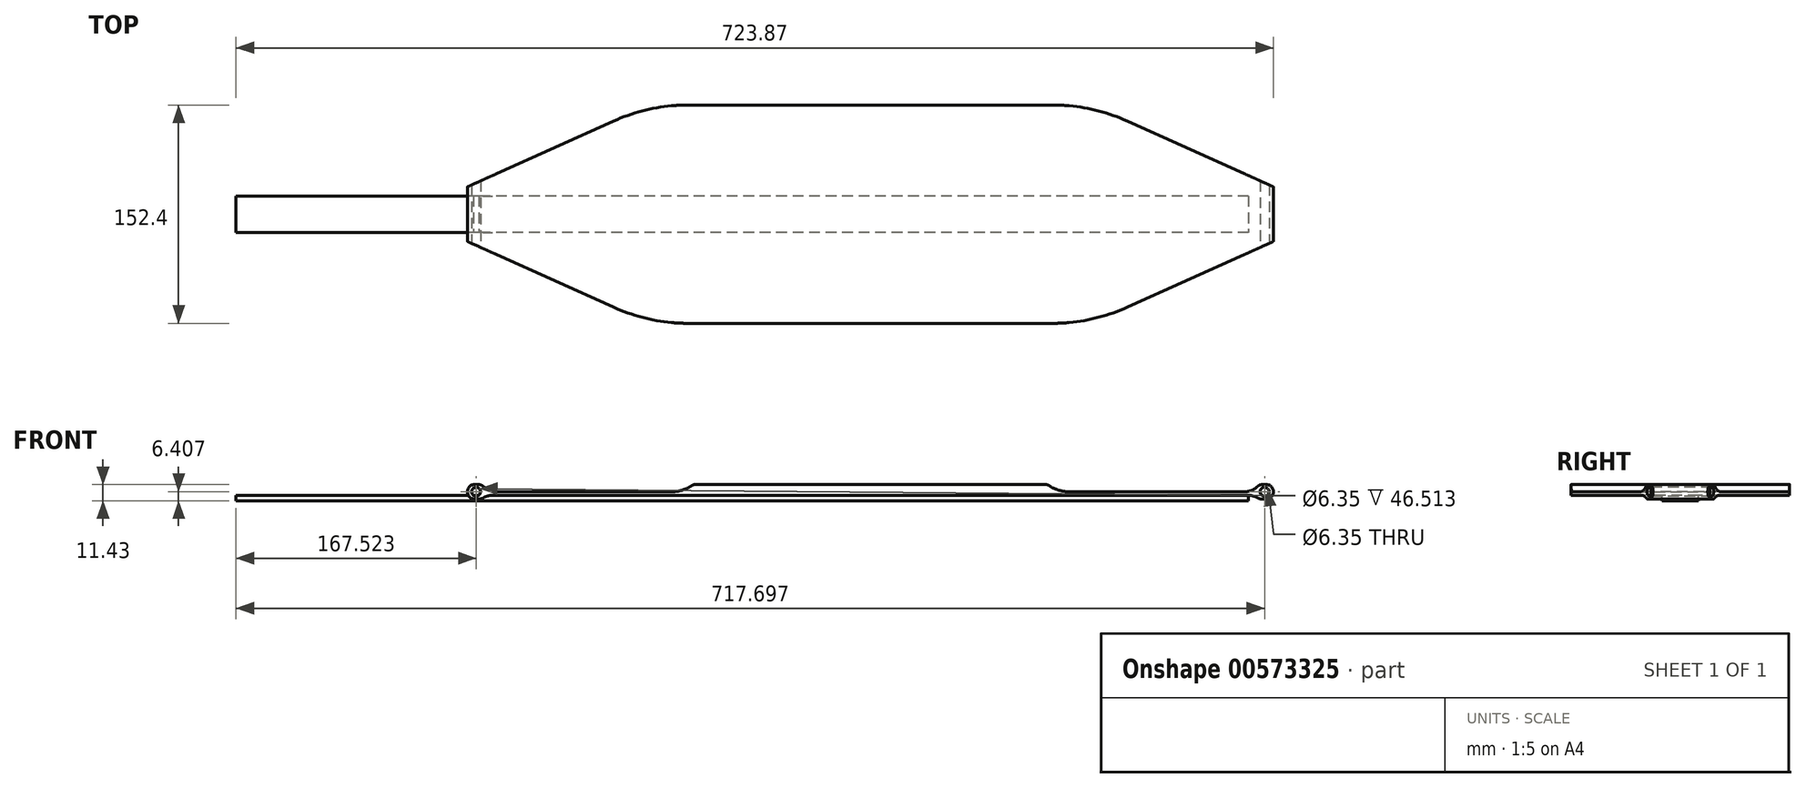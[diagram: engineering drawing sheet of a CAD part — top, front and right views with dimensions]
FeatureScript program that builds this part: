
annotation { "Feature Type Name" : "Feature", "Feature Type Description" : "" }
export const myFeature = defineFeature(function(context is Context, id is Id, definition is map)
    precondition{}
    {
        {
            var Q0;
            Q0=qCreatedBy(makeId("Top.planeOp"),FACE);
            var sketch = newSketch(context, id + "F0", { "sketchPlane" : qUnion([Q0])});
            skLineSegment(sketch, "E0", {"start": v(0, 76.2) * mm, "end": v(-127, 76.2) * mm});
            skLineSegment(sketch, "E1", {"start": v(-179.12, 65.01) * mm, "end": v(-281.26, 19.05) * mm});
            skLineSegment(sketch, "E2", {"start": v(-281.26, 19.05) * mm, "end": v(-281.26, 0) * mm});
            skLineSegment(sketch, "E3", {"start": v(-281.26, 0) * mm, "end": v(-281.26, -19.05) * mm});
            skLineSegment(sketch, "E4", {"start": v(-281.26, -19.05) * mm, "end": v(-179.12, -65.01) * mm});
            skLineSegment(sketch, "E5", {"start": v(-127, -76.2) * mm, "end": v(0, -76.2) * mm});
            skPoint(sketch, "E6.visualSharp", {"position": v(-154.26, 76.2) * mm});
            skArc(sketch, "E6.filletArc", {"start": v(-127, 76.2) * mm, "mid": v(-153.65, 73.37) * mm, "end": v(-179.12, 65.01) * mm});
            skPoint(sketch, "E7.visualSharp", {"position": v(-154.26, -76.2) * mm});
            skArc(sketch, "E7.filletArc", {"start": v(-179.12, -65.01) * mm, "mid": v(-153.65, -73.37) * mm, "end": v(-127, -76.2) * mm});
            skLineSegment(sketch, "E8.MirrorCS", {"start": v(0, 76.2) * mm, "end": v(127, 76.2) * mm});
            skLineSegment(sketch, "E9.MirrorCS", {"start": v(179.12, 65.01) * mm, "end": v(281.26, 19.05) * mm});
            skLineSegment(sketch, "E10.MirrorCS", {"start": v(281.26, 19.05) * mm, "end": v(281.26, 0) * mm});
            skLineSegment(sketch, "E11.MirrorCS", {"start": v(281.26, 0) * mm, "end": v(281.26, -19.05) * mm});
            skPoint(sketch, "E12.MirrorP", {"position": v(154.26, -76.2) * mm});
            skLineSegment(sketch, "E13.MirrorCS", {"start": v(281.26, -19.05) * mm, "end": v(179.12, -65.01) * mm});
            skArc(sketch, "E14.MirrorCS", {"start": v(179.12, -65.01) * mm, "mid": v(153.65, -73.37) * mm, "end": v(127, -76.2) * mm});
            skLineSegment(sketch, "E15.MirrorCS", {"start": v(127, -76.2) * mm, "end": v(0, -76.2) * mm});
            skArc(sketch, "E16.MirrorCS", {"start": v(127, 76.2) * mm, "mid": v(153.65, 73.37) * mm, "end": v(179.12, 65.01) * mm});
            skPoint(sketch, "E17.MirrorP", {"position": v(154.26, 76.2) * mm});
            skSolve(sketch);
        }
        {
            var Q0;
            Q0 = qSketchRegion(id + "F0", true);
            extrude(context, id + "F1", {"entities" : qUnion([Q0]), "depth" : 2.54 * mm, "offsetDistance" : 25.4 * mm});
        }
        {
            var Q0;
            Q0=makeQuery(id+"F1.opExtrude","CAP_FACE",FACE,{"disambiguationData":[OSD([sQuery(id+"F0.wireOp",EDGE,"E0"),sQuery(id+"F0.wireOp",EDGE,"E1"),sQuery(id+"F0.wireOp",EDGE,"E2"),sQuery(id+"F0.wireOp",EDGE,"E3"),sQuery(id+"F0.wireOp",EDGE,"E4"),sQuery(id+"F0.wireOp",EDGE,"E5"),sQuery(id+"F0.wireOp",EDGE,"E6.filletArc"),sQuery(id+"F0.wireOp",EDGE,"E7.filletArc"),sQuery(id+"F0.wireOp",EDGE,"E8.MirrorCS"),sQuery(id+"F0.wireOp",EDGE,"E9.MirrorCS"),sQuery(id+"F0.wireOp",EDGE,"E10.MirrorCS"),sQuery(id+"F0.wireOp",EDGE,"E11.MirrorCS"),sQuery(id+"F0.wireOp",EDGE,"E13.MirrorCS"),sQuery(id+"F0.wireOp",EDGE,"E14.MirrorCS"),sQuery(id+"F0.wireOp",EDGE,"E15.MirrorCS"),sQuery(id+"F0.wireOp",EDGE,"E16.MirrorCS")])],"isStart":false});
            var sketch = newSketch(context, id + "F2", { "sketchPlane" : qUnion([Q0])});
            skLineSegment(sketch, "E18", {"start": v(0, 76.2) * mm, "end": v(-127, 76.2) * mm});
            skLineSegment(sketch, "E19", {"start": v(-127, -76.2) * mm, "end": v(0, -76.2) * mm});
            skLineSegment(sketch, "E20.MirrorCS", {"start": v(127, -76.2) * mm, "end": v(0, -76.2) * mm});
            skLineSegment(sketch, "E21.MirrorCS", {"start": v(0, 76.2) * mm, "end": v(127, 76.2) * mm});
            skLineSegment(sketch, "E22", {"start": v(-127, 76.2) * mm, "end": v(-127, -76.2) * mm});
            skLineSegment(sketch, "E23", {"start": v(127, 76.2) * mm, "end": v(127, -76.2) * mm});
            skSolve(sketch);
        }
        {
            var Q0;
            Q0 = qSketchRegion(id + "F2", true);
            extrude(context, id + "F3", {"entities" : qUnion([Q0]), "operationType" : NewBodyOperationType.ADD, "depth" : 5.08 * mm, "offsetDistance" : 25.4 * mm});
        }
        {
            var Q0;
            Q0=makeQuery(id+"F3.opExtrude","CAP_EDGE",EDGE,{"disambiguationData":[OSD([sQuery(id+"F2.wireOp",EDGE,"E22")])],"isStart":false});
            var Q1;
            Q1=makeQuery(id+"F3.opExtrude","CAP_EDGE",EDGE,{"disambiguationData":[OSD([sQuery(id+"F2.wireOp",EDGE,"E23")])],"isStart":false});
            fillet(context, id + "F4", {"entities" : qUnion([Q0, Q1]), "radius" : 5.08 * mm, "tangentPropagation" : true, "allowEdgeOverflow" : false});
        }
        {
            var Q0;
            {var subQ0=sQuery(id+"F0.wireOp",EDGE,"E4");var subQ1=sQuery(id+"F2.wireOp",EDGE,"E22");var subQ2=sQuery(id+"F0.wireOp",EDGE,"E3");var subQ3=sQuery(id+"F0.wireOp",EDGE,"E2");var subQ4=sQuery(id+"F0.wireOp",EDGE,"E1");var subQ5=sQuery(id+"F0.wireOp",EDGE,"E8.MirrorCS");var subQ6=sQuery(id+"F0.wireOp",EDGE,"E0");var subQ7=sQuery(id+"F0.wireOp",EDGE,"E15.MirrorCS");var subQ8=sQuery(id+"F0.wireOp",EDGE,"E5");var subQ9=sQuery(id+"F0.wireOp",EDGE,"E6.filletArc");var subQ10=sQuery(id+"F0.wireOp",EDGE,"E7.filletArc");Q0=makeQuery(id+"F4.opFillet","BLEND_EDGE",EDGE,{"blendedFrom":[makeQuery(id+"F3.opExtrude","CAP_EDGE",EDGE,{"disambiguationData":[OSD([subQ1])],"isStart":false}),makeQuery(id+"F3.boolean.opBoolean","SPLIT",FACE,{"disambiguationData":[TD([makeQuery(id+"F1.opExtrude","SWEPT_FACE",FACE,{"disambiguationData":[OSD([subQ4])]})])],"derivedFrom":makeQuery(id+"F1.opExtrude","CAP_FACE",FACE,{"disambiguationData":[OSD([subQ6,subQ4,subQ3,subQ2,subQ0,subQ8,subQ9,subQ10,subQ5,sQuery(id+"F0.wireOp",EDGE,"E9.MirrorCS"),sQuery(id+"F0.wireOp",EDGE,"E10.MirrorCS"),sQuery(id+"F0.wireOp",EDGE,"E11.MirrorCS"),sQuery(id+"F0.wireOp",EDGE,"E13.MirrorCS"),sQuery(id+"F0.wireOp",EDGE,"E14.MirrorCS"),subQ7,sQuery(id+"F0.wireOp",EDGE,"E16.MirrorCS")])],"isStart":false})})],"blendedInto":[makeQuery(id+"F3.boolean.opBoolean","SPLIT",FACE,{"disambiguationData":[TD([makeQuery(id+"F1.opExtrude","SWEPT_FACE",FACE,{"disambiguationData":[OSD([subQ4])]})])],"derivedFrom":makeQuery(id+"F1.opExtrude","CAP_FACE",FACE,{"disambiguationData":[OSD([subQ6,subQ4,subQ3,subQ2,subQ0,subQ8,subQ9,subQ10,subQ5,sQuery(id+"F0.wireOp",EDGE,"E9.MirrorCS"),sQuery(id+"F0.wireOp",EDGE,"E10.MirrorCS"),sQuery(id+"F0.wireOp",EDGE,"E11.MirrorCS"),sQuery(id+"F0.wireOp",EDGE,"E13.MirrorCS"),sQuery(id+"F0.wireOp",EDGE,"E14.MirrorCS"),subQ7,sQuery(id+"F0.wireOp",EDGE,"E16.MirrorCS")])],"isStart":false})})]});}
            var Q1;
            {var subQ0=sQuery(id+"F0.wireOp",EDGE,"E11.MirrorCS");var subQ1=sQuery(id+"F0.wireOp",EDGE,"E10.MirrorCS");var subQ2=sQuery(id+"F0.wireOp",EDGE,"E9.MirrorCS");var subQ3=sQuery(id+"F0.wireOp",EDGE,"E15.MirrorCS");var subQ4=sQuery(id+"F0.wireOp",EDGE,"E5");var subQ5=sQuery(id+"F2.wireOp",EDGE,"E23");var subQ6=sQuery(id+"F0.wireOp",EDGE,"E8.MirrorCS");var subQ7=sQuery(id+"F0.wireOp",EDGE,"E0");var subQ8=sQuery(id+"F0.wireOp",EDGE,"E16.MirrorCS");var subQ9=sQuery(id+"F0.wireOp",EDGE,"E13.MirrorCS");var subQ10=sQuery(id+"F0.wireOp",EDGE,"E14.MirrorCS");Q1=makeQuery(id+"F4.opFillet","BLEND_EDGE",EDGE,{"blendedFrom":[makeQuery(id+"F3.opExtrude","CAP_EDGE",EDGE,{"disambiguationData":[OSD([subQ5])],"isStart":false}),makeQuery(id+"F3.boolean.opBoolean","SPLIT",FACE,{"disambiguationData":[TD([makeQuery(id+"F1.opExtrude","SWEPT_FACE",FACE,{"disambiguationData":[OSD([subQ2])]})])],"derivedFrom":makeQuery(id+"F1.opExtrude","CAP_FACE",FACE,{"disambiguationData":[OSD([subQ7,sQuery(id+"F0.wireOp",EDGE,"E1"),sQuery(id+"F0.wireOp",EDGE,"E2"),sQuery(id+"F0.wireOp",EDGE,"E3"),sQuery(id+"F0.wireOp",EDGE,"E4"),subQ4,sQuery(id+"F0.wireOp",EDGE,"E6.filletArc"),sQuery(id+"F0.wireOp",EDGE,"E7.filletArc"),subQ6,subQ2,subQ1,subQ0,subQ9,subQ10,subQ3,subQ8])],"isStart":false})})],"blendedInto":[makeQuery(id+"F3.boolean.opBoolean","SPLIT",FACE,{"disambiguationData":[TD([makeQuery(id+"F1.opExtrude","SWEPT_FACE",FACE,{"disambiguationData":[OSD([subQ2])]})])],"derivedFrom":makeQuery(id+"F1.opExtrude","CAP_FACE",FACE,{"disambiguationData":[OSD([subQ7,sQuery(id+"F0.wireOp",EDGE,"E1"),sQuery(id+"F0.wireOp",EDGE,"E2"),sQuery(id+"F0.wireOp",EDGE,"E3"),sQuery(id+"F0.wireOp",EDGE,"E4"),subQ4,sQuery(id+"F0.wireOp",EDGE,"E6.filletArc"),sQuery(id+"F0.wireOp",EDGE,"E7.filletArc"),subQ6,subQ2,subQ1,subQ0,subQ9,subQ10,subQ3,subQ8])],"isStart":false})})]});}
            fillet(context, id + "F5", {"entities" : qUnion([Q0, Q1]), "radius" : 25.4 * mm, "tangentPropagation" : true, "allowEdgeOverflow" : false});
        }
        {
            var Q0;
            {var subQ0=sQuery(id+"F0.wireOp",EDGE,"E4");var subQ1=sQuery(id+"F0.wireOp",EDGE,"E3");var subQ2=sQuery(id+"F0.wireOp",EDGE,"E2");var subQ3=sQuery(id+"F0.wireOp",EDGE,"E1");var subQ4=sQuery(id+"F0.wireOp",EDGE,"E8.MirrorCS");var subQ5=sQuery(id+"F0.wireOp",EDGE,"E0");var subQ6=sQuery(id+"F0.wireOp",EDGE,"E15.MirrorCS");var subQ7=sQuery(id+"F0.wireOp",EDGE,"E5");var subQ8=sQuery(id+"F0.wireOp",EDGE,"E6.filletArc");var subQ9=sQuery(id+"F0.wireOp",EDGE,"E7.filletArc");Q0=makeQuery(id+"F3.boolean.opBoolean","SPLIT",FACE,{"disambiguationData":[TD([makeQuery(id+"F1.opExtrude","SWEPT_FACE",FACE,{"disambiguationData":[OSD([subQ3])]})])],"derivedFrom":makeQuery(id+"F1.opExtrude","CAP_FACE",FACE,{"disambiguationData":[OSD([subQ5,subQ3,subQ2,subQ1,subQ0,subQ7,subQ8,subQ9,subQ4,sQuery(id+"F0.wireOp",EDGE,"E9.MirrorCS"),sQuery(id+"F0.wireOp",EDGE,"E10.MirrorCS"),sQuery(id+"F0.wireOp",EDGE,"E11.MirrorCS"),sQuery(id+"F0.wireOp",EDGE,"E13.MirrorCS"),sQuery(id+"F0.wireOp",EDGE,"E14.MirrorCS"),subQ6,sQuery(id+"F0.wireOp",EDGE,"E16.MirrorCS")])],"isStart":false})});}
            var sketch = newSketch(context, id + "F6", { "sketchPlane" : qUnion([Q0])});
            skLineSegment(sketch, "E24", {"start": v(-281.26, 19.05) * mm, "end": v(-268.56, 24.76) * mm});
            skLineSegment(sketch, "E25", {"start": v(-268.56, 24.76) * mm, "end": v(-268.56, -24.76) * mm});
            skLineSegment(sketch, "E26", {"start": v(-268.56, -24.76) * mm, "end": v(-281.26, -19.05) * mm});
            skLineSegment(sketch, "E27", {"start": v(-281.26, -19.05) * mm, "end": v(-281.26, 19.05) * mm});
            skLineSegment(sketch, "E28.MirrorCS", {"start": v(268.56, 24.76) * mm, "end": v(268.56, -24.76) * mm});
            skLineSegment(sketch, "E29.MirrorCS", {"start": v(268.56, -24.76) * mm, "end": v(281.26, -19.05) * mm});
            skLineSegment(sketch, "E30.MirrorCS", {"start": v(281.26, -19.05) * mm, "end": v(281.26, 19.05) * mm});
            skLineSegment(sketch, "E31.MirrorCS", {"start": v(281.26, 19.05) * mm, "end": v(268.56, 24.76) * mm});
            skSolve(sketch);
        }
        {
            var Q0;
            Q0 = qSketchRegion(id + "F6", true);
            extrude(context, id + "F7", {"entities" : qUnion([Q0]), "operationType" : NewBodyOperationType.ADD, "depth" : 5.08 * mm, "offsetDistance" : 25.4 * mm, "hasSecondDirection" : true, "secondDirectionOppositeDirection" : true, "secondDirectionDepth" : 5.08 * mm});
        }
        {
            var Q0;
            Q0=qCreatedBy(makeId("Front.planeOp"),FACE);
            var sketch = newSketch(context, id + "F8", { "sketchPlane" : qUnion([Q0])});
            skCircle(sketch, "E32", {"center": v(-275.09, 2.6) * mm, "radius": 3.18 * mm});
            skCircle(sketch, "E33.MirrorC", {"center": v(275.09, 2.6) * mm, "radius": 3.18 * mm});
            skSolve(sketch);
        }
        {
            var Q0;
            Q0 = qSketchRegion(id + "F8", true);
            extrude(context, id + "F9", {"entities" : qUnion([Q0]), "operationType" : NewBodyOperationType.REMOVE, "endBound" : BoundingType.THROUGH_ALL, "oppositeDirection" : true, "depth" : 25.4 * mm, "offsetDistance" : 25.4 * mm, "hasSecondDirection" : true, "secondDirectionBound" : SecondDirectionBoundingType.THROUGH_ALL, "secondDirectionOppositeDirection" : false, "secondDirectionDepth" : 25.4 * mm});
        }
        {
            var Q0;
            Q0=makeQuery(id+"F7.opExtrude","CAP_EDGE",EDGE,{"disambiguationData":[OSD([sQuery(id+"F6.wireOp",EDGE,"E27")])],"isStart":false});
            var Q1;
            Q1=makeQuery(id+"F7.opExtrude","CAP_EDGE",EDGE,{"disambiguationData":[OSD([sQuery(id+"F6.wireOp",EDGE,"E27")])],"isStart":true});
            var Q2;
            Q2=makeQuery(id+"F7.opExtrude","CAP_EDGE",EDGE,{"disambiguationData":[OSD([sQuery(id+"F6.wireOp",EDGE,"E25")])],"isStart":true});
            var Q3;
            Q3=makeQuery(id+"F7.opExtrude","CAP_EDGE",EDGE,{"disambiguationData":[OSD([sQuery(id+"F6.wireOp",EDGE,"E25")])],"isStart":false});
            var Q4;
            Q4=makeQuery(id+"F7.opExtrude","CAP_EDGE",EDGE,{"disambiguationData":[OSD([sQuery(id+"F6.wireOp",EDGE,"E28.MirrorCS")])],"isStart":false});
            var Q5;
            Q5=makeQuery(id+"F7.opExtrude","CAP_EDGE",EDGE,{"disambiguationData":[OSD([sQuery(id+"F6.wireOp",EDGE,"E30.MirrorCS")])],"isStart":false});
            var Q6;
            Q6=makeQuery(id+"F7.opExtrude","CAP_EDGE",EDGE,{"disambiguationData":[OSD([sQuery(id+"F6.wireOp",EDGE,"E30.MirrorCS")])],"isStart":true});
            var Q7;
            Q7=makeQuery(id+"F7.opExtrude","CAP_EDGE",EDGE,{"disambiguationData":[OSD([sQuery(id+"F6.wireOp",EDGE,"E28.MirrorCS")])],"isStart":true});
            fillet(context, id + "F10", {"entities" : qUnion([Q0, Q1, Q2, Q3, Q4, Q5, Q6, Q7]), "radius" : 5.08 * mm, "tangentPropagation" : true, "allowEdgeOverflow" : false});
        }
        {
            var Q0;
            {var subQ0=sQuery(id+"F0.wireOp",EDGE,"E4");var subQ1=sQuery(id+"F0.wireOp",EDGE,"E3");var subQ2=sQuery(id+"F0.wireOp",EDGE,"E2");var subQ3=sQuery(id+"F0.wireOp",EDGE,"E1");var subQ4=sQuery(id+"F0.wireOp",EDGE,"E8.MirrorCS");var subQ5=sQuery(id+"F0.wireOp",EDGE,"E0");var subQ6=sQuery(id+"F0.wireOp",EDGE,"E15.MirrorCS");var subQ7=sQuery(id+"F0.wireOp",EDGE,"E5");var subQ8=sQuery(id+"F0.wireOp",EDGE,"E6.filletArc");var subQ9=sQuery(id+"F0.wireOp",EDGE,"E7.filletArc");Q0=makeQuery(id+"F10.opFillet","BLEND_EDGE",EDGE,{"blendedFrom":[makeQuery(id+"F7.opExtrude","CAP_EDGE",EDGE,{"disambiguationData":[OSD([sQuery(id+"F6.wireOp",EDGE,"E25")])],"isStart":false}),makeQuery(id+"F3.boolean.opBoolean","SPLIT",FACE,{"disambiguationData":[TD([makeQuery(id+"F1.opExtrude","SWEPT_FACE",FACE,{"disambiguationData":[OSD([subQ3])]})])],"derivedFrom":makeQuery(id+"F1.opExtrude","CAP_FACE",FACE,{"disambiguationData":[OSD([subQ5,subQ3,subQ2,subQ1,subQ0,subQ7,subQ8,subQ9,subQ4,sQuery(id+"F0.wireOp",EDGE,"E9.MirrorCS"),sQuery(id+"F0.wireOp",EDGE,"E10.MirrorCS"),sQuery(id+"F0.wireOp",EDGE,"E11.MirrorCS"),sQuery(id+"F0.wireOp",EDGE,"E13.MirrorCS"),sQuery(id+"F0.wireOp",EDGE,"E14.MirrorCS"),subQ6,sQuery(id+"F0.wireOp",EDGE,"E16.MirrorCS")])],"isStart":false})})],"blendedInto":[makeQuery(id+"F3.boolean.opBoolean","SPLIT",FACE,{"disambiguationData":[TD([makeQuery(id+"F1.opExtrude","SWEPT_FACE",FACE,{"disambiguationData":[OSD([subQ3])]})])],"derivedFrom":makeQuery(id+"F1.opExtrude","CAP_FACE",FACE,{"disambiguationData":[OSD([subQ5,subQ3,subQ2,subQ1,subQ0,subQ7,subQ8,subQ9,subQ4,sQuery(id+"F0.wireOp",EDGE,"E9.MirrorCS"),sQuery(id+"F0.wireOp",EDGE,"E10.MirrorCS"),sQuery(id+"F0.wireOp",EDGE,"E11.MirrorCS"),sQuery(id+"F0.wireOp",EDGE,"E13.MirrorCS"),sQuery(id+"F0.wireOp",EDGE,"E14.MirrorCS"),subQ6,sQuery(id+"F0.wireOp",EDGE,"E16.MirrorCS")])],"isStart":false})})]});}
            var Q1;
            Q1=makeQuery(id+"F10.opFillet","BLEND_EDGE",EDGE,{"blendedFrom":[makeQuery(id+"F7.opExtrude","CAP_EDGE",EDGE,{"disambiguationData":[OSD([sQuery(id+"F6.wireOp",EDGE,"E25")])],"isStart":true}),makeQuery(id+"F1.opExtrude","CAP_FACE",FACE,{"disambiguationData":[OSD([sQuery(id+"F0.wireOp",EDGE,"E0"),sQuery(id+"F0.wireOp",EDGE,"E1"),sQuery(id+"F0.wireOp",EDGE,"E2"),sQuery(id+"F0.wireOp",EDGE,"E3"),sQuery(id+"F0.wireOp",EDGE,"E4"),sQuery(id+"F0.wireOp",EDGE,"E5"),sQuery(id+"F0.wireOp",EDGE,"E6.filletArc"),sQuery(id+"F0.wireOp",EDGE,"E7.filletArc"),sQuery(id+"F0.wireOp",EDGE,"E8.MirrorCS"),sQuery(id+"F0.wireOp",EDGE,"E9.MirrorCS"),sQuery(id+"F0.wireOp",EDGE,"E10.MirrorCS"),sQuery(id+"F0.wireOp",EDGE,"E11.MirrorCS"),sQuery(id+"F0.wireOp",EDGE,"E13.MirrorCS"),sQuery(id+"F0.wireOp",EDGE,"E14.MirrorCS"),sQuery(id+"F0.wireOp",EDGE,"E15.MirrorCS"),sQuery(id+"F0.wireOp",EDGE,"E16.MirrorCS")])],"isStart":true})],"blendedInto":[makeQuery(id+"F1.opExtrude","CAP_FACE",FACE,{"disambiguationData":[OSD([sQuery(id+"F0.wireOp",EDGE,"E0"),sQuery(id+"F0.wireOp",EDGE,"E1"),sQuery(id+"F0.wireOp",EDGE,"E2"),sQuery(id+"F0.wireOp",EDGE,"E3"),sQuery(id+"F0.wireOp",EDGE,"E4"),sQuery(id+"F0.wireOp",EDGE,"E5"),sQuery(id+"F0.wireOp",EDGE,"E6.filletArc"),sQuery(id+"F0.wireOp",EDGE,"E7.filletArc"),sQuery(id+"F0.wireOp",EDGE,"E8.MirrorCS"),sQuery(id+"F0.wireOp",EDGE,"E9.MirrorCS"),sQuery(id+"F0.wireOp",EDGE,"E10.MirrorCS"),sQuery(id+"F0.wireOp",EDGE,"E11.MirrorCS"),sQuery(id+"F0.wireOp",EDGE,"E13.MirrorCS"),sQuery(id+"F0.wireOp",EDGE,"E14.MirrorCS"),sQuery(id+"F0.wireOp",EDGE,"E15.MirrorCS"),sQuery(id+"F0.wireOp",EDGE,"E16.MirrorCS")])],"isStart":true})]});
            var Q2;
            {var subQ0=sQuery(id+"F0.wireOp",EDGE,"E11.MirrorCS");var subQ1=sQuery(id+"F0.wireOp",EDGE,"E10.MirrorCS");var subQ2=sQuery(id+"F0.wireOp",EDGE,"E9.MirrorCS");var subQ3=sQuery(id+"F0.wireOp",EDGE,"E15.MirrorCS");var subQ4=sQuery(id+"F0.wireOp",EDGE,"E5");var subQ5=sQuery(id+"F0.wireOp",EDGE,"E8.MirrorCS");var subQ6=sQuery(id+"F0.wireOp",EDGE,"E0");var subQ7=sQuery(id+"F0.wireOp",EDGE,"E16.MirrorCS");var subQ8=sQuery(id+"F0.wireOp",EDGE,"E13.MirrorCS");var subQ9=sQuery(id+"F0.wireOp",EDGE,"E14.MirrorCS");Q2=makeQuery(id+"F10.opFillet","BLEND_EDGE",EDGE,{"blendedFrom":[makeQuery(id+"F7.opExtrude","CAP_EDGE",EDGE,{"disambiguationData":[OSD([sQuery(id+"F6.wireOp",EDGE,"E28.MirrorCS")])],"isStart":false}),makeQuery(id+"F3.boolean.opBoolean","SPLIT",FACE,{"disambiguationData":[TD([makeQuery(id+"F1.opExtrude","SWEPT_FACE",FACE,{"disambiguationData":[OSD([subQ2])]})])],"derivedFrom":makeQuery(id+"F1.opExtrude","CAP_FACE",FACE,{"disambiguationData":[OSD([subQ6,sQuery(id+"F0.wireOp",EDGE,"E1"),sQuery(id+"F0.wireOp",EDGE,"E2"),sQuery(id+"F0.wireOp",EDGE,"E3"),sQuery(id+"F0.wireOp",EDGE,"E4"),subQ4,sQuery(id+"F0.wireOp",EDGE,"E6.filletArc"),sQuery(id+"F0.wireOp",EDGE,"E7.filletArc"),subQ5,subQ2,subQ1,subQ0,subQ8,subQ9,subQ3,subQ7])],"isStart":false})})],"blendedInto":[makeQuery(id+"F3.boolean.opBoolean","SPLIT",FACE,{"disambiguationData":[TD([makeQuery(id+"F1.opExtrude","SWEPT_FACE",FACE,{"disambiguationData":[OSD([subQ2])]})])],"derivedFrom":makeQuery(id+"F1.opExtrude","CAP_FACE",FACE,{"disambiguationData":[OSD([subQ6,sQuery(id+"F0.wireOp",EDGE,"E1"),sQuery(id+"F0.wireOp",EDGE,"E2"),sQuery(id+"F0.wireOp",EDGE,"E3"),sQuery(id+"F0.wireOp",EDGE,"E4"),subQ4,sQuery(id+"F0.wireOp",EDGE,"E6.filletArc"),sQuery(id+"F0.wireOp",EDGE,"E7.filletArc"),subQ5,subQ2,subQ1,subQ0,subQ8,subQ9,subQ3,subQ7])],"isStart":false})})]});}
            var Q3;
            Q3=makeQuery(id+"F10.opFillet","BLEND_EDGE",EDGE,{"blendedFrom":[makeQuery(id+"F7.opExtrude","CAP_EDGE",EDGE,{"disambiguationData":[OSD([sQuery(id+"F6.wireOp",EDGE,"E28.MirrorCS")])],"isStart":true}),makeQuery(id+"F1.opExtrude","CAP_FACE",FACE,{"disambiguationData":[OSD([sQuery(id+"F0.wireOp",EDGE,"E0"),sQuery(id+"F0.wireOp",EDGE,"E1"),sQuery(id+"F0.wireOp",EDGE,"E2"),sQuery(id+"F0.wireOp",EDGE,"E3"),sQuery(id+"F0.wireOp",EDGE,"E4"),sQuery(id+"F0.wireOp",EDGE,"E5"),sQuery(id+"F0.wireOp",EDGE,"E6.filletArc"),sQuery(id+"F0.wireOp",EDGE,"E7.filletArc"),sQuery(id+"F0.wireOp",EDGE,"E8.MirrorCS"),sQuery(id+"F0.wireOp",EDGE,"E9.MirrorCS"),sQuery(id+"F0.wireOp",EDGE,"E10.MirrorCS"),sQuery(id+"F0.wireOp",EDGE,"E11.MirrorCS"),sQuery(id+"F0.wireOp",EDGE,"E13.MirrorCS"),sQuery(id+"F0.wireOp",EDGE,"E14.MirrorCS"),sQuery(id+"F0.wireOp",EDGE,"E15.MirrorCS"),sQuery(id+"F0.wireOp",EDGE,"E16.MirrorCS")])],"isStart":true})],"blendedInto":[makeQuery(id+"F1.opExtrude","CAP_FACE",FACE,{"disambiguationData":[OSD([sQuery(id+"F0.wireOp",EDGE,"E0"),sQuery(id+"F0.wireOp",EDGE,"E1"),sQuery(id+"F0.wireOp",EDGE,"E2"),sQuery(id+"F0.wireOp",EDGE,"E3"),sQuery(id+"F0.wireOp",EDGE,"E4"),sQuery(id+"F0.wireOp",EDGE,"E5"),sQuery(id+"F0.wireOp",EDGE,"E6.filletArc"),sQuery(id+"F0.wireOp",EDGE,"E7.filletArc"),sQuery(id+"F0.wireOp",EDGE,"E8.MirrorCS"),sQuery(id+"F0.wireOp",EDGE,"E9.MirrorCS"),sQuery(id+"F0.wireOp",EDGE,"E10.MirrorCS"),sQuery(id+"F0.wireOp",EDGE,"E11.MirrorCS"),sQuery(id+"F0.wireOp",EDGE,"E13.MirrorCS"),sQuery(id+"F0.wireOp",EDGE,"E14.MirrorCS"),sQuery(id+"F0.wireOp",EDGE,"E15.MirrorCS"),sQuery(id+"F0.wireOp",EDGE,"E16.MirrorCS")])],"isStart":true})]});
            fillet(context, id + "F11", {"entities" : qUnion([Q0, Q1, Q2, Q3]), "radius" : 12.7 * mm, "tangentPropagation" : true, "allowEdgeOverflow" : false});
        }
        {
            var Q0;
            Q0=makeQuery(id+"F1.opExtrude","CAP_FACE",FACE,{"disambiguationData":[OSD([sQuery(id+"F0.wireOp",EDGE,"E0"),sQuery(id+"F0.wireOp",EDGE,"E1"),sQuery(id+"F0.wireOp",EDGE,"E2"),sQuery(id+"F0.wireOp",EDGE,"E3"),sQuery(id+"F0.wireOp",EDGE,"E4"),sQuery(id+"F0.wireOp",EDGE,"E5"),sQuery(id+"F0.wireOp",EDGE,"E6.filletArc"),sQuery(id+"F0.wireOp",EDGE,"E7.filletArc"),sQuery(id+"F0.wireOp",EDGE,"E8.MirrorCS"),sQuery(id+"F0.wireOp",EDGE,"E9.MirrorCS"),sQuery(id+"F0.wireOp",EDGE,"E10.MirrorCS"),sQuery(id+"F0.wireOp",EDGE,"E11.MirrorCS"),sQuery(id+"F0.wireOp",EDGE,"E13.MirrorCS"),sQuery(id+"F0.wireOp",EDGE,"E14.MirrorCS"),sQuery(id+"F0.wireOp",EDGE,"E15.MirrorCS"),sQuery(id+"F0.wireOp",EDGE,"E16.MirrorCS")])],"isStart":true});
            var sketch = newSketch(context, id + "F12", { "sketchPlane" : qUnion([Q0])});
            skLineSegment(sketch, "E34.bottom", {"start": v(263.8, -12.7) * mm, "end": v(-263.8, -12.7) * mm});
            skLineSegment(sketch, "E34.top", {"start": v(263.8, 12.7) * mm, "end": v(-263.8, 12.7) * mm});
            skLineSegment(sketch, "E34.left", {"start": v(263.8, -12.7) * mm, "end": v(263.8, 12.7) * mm});
            skPoint(sketch, "E34.middle", {"position": v(0, 0) * mm});
            skLineSegment(sketch, "E35.bottom", {"start": v(-263.8, 12.7) * mm, "end": v(-442.6, 12.7) * mm});
            skLineSegment(sketch, "E35.top", {"start": v(-263.8, -12.7) * mm, "end": v(-442.6, -12.7) * mm});
            skLineSegment(sketch, "E35.right", {"start": v(-442.6, 12.7) * mm, "end": v(-442.6, -12.7) * mm});
            skSolve(sketch);
        }
        {
            var Q0;
            Q0 = qSketchRegion(id + "F12", true);
            extrude(context, id + "F13", {"entities" : qUnion([Q0]), "operationType" : NewBodyOperationType.ADD, "depth" : 3.8 * mm, "offsetDistance" : 25.4 * mm});
        }
    });
